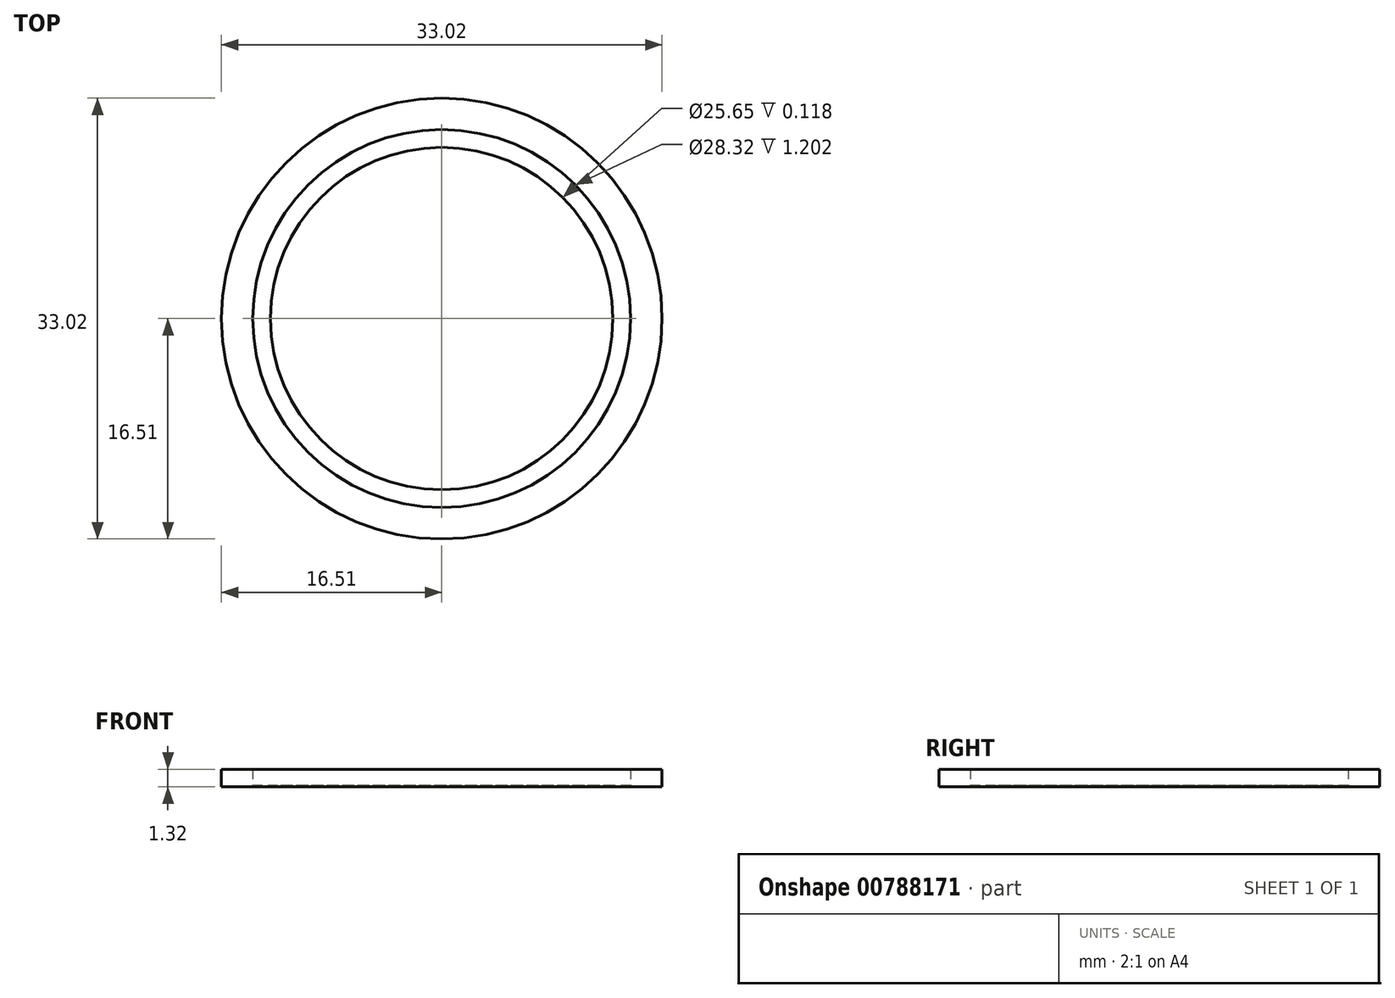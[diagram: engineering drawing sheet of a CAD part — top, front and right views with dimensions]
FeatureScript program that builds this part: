
annotation { "Feature Type Name" : "Feature", "Feature Type Description" : "" }
export const myFeature = defineFeature(function(context is Context, id is Id, definition is map)
    precondition{}
    {
        {
            var Q0;
            Q0=qCreatedBy(makeId("Top.planeOp"),FACE);
            var sketch = newSketch(context, id + "F0", { "sketchPlane" : qUnion([Q0])});
            skCircle(sketch, "E0", {"center": v(0, 0) * mm, "radius": 12.83 * mm});
            skCircle(sketch, "E1", {"center": v(0, 0) * mm, "radius": 14.16 * mm});
            skCircle(sketch, "E2", {"center": v(0, 0) * mm, "radius": 16.51 * mm});
            skSolve(sketch);
        }
        {
            var Q0;
            Q0=makeQuery(id+"F0.imprint","IMPRINT",FACE,{"disambiguationData":[TD([[makeQuery(id+"F0.imprint","IMPRINT",EDGE,{"derivedFrom":sQuery(id+"F0.wireOp",EDGE,"E0")}),-1.0]])]});
            extrude(context, id + "F1", {"entities" : qUnion([Q0]), "depth" : ((0.14 / 2) + 0.05) * mm, "offsetDistance" : 25.4 * mm});
        }
        {
            var Q0;
            Q0 = qSketchRegion(id + "F0", true);
            extrude(context, id + "F2", {"entities" : qUnion([Q0]), "operationType" : NewBodyOperationType.ADD, "depth" : 1.32 * mm, "offsetDistance" : 25.4 * mm});
        }
    });
